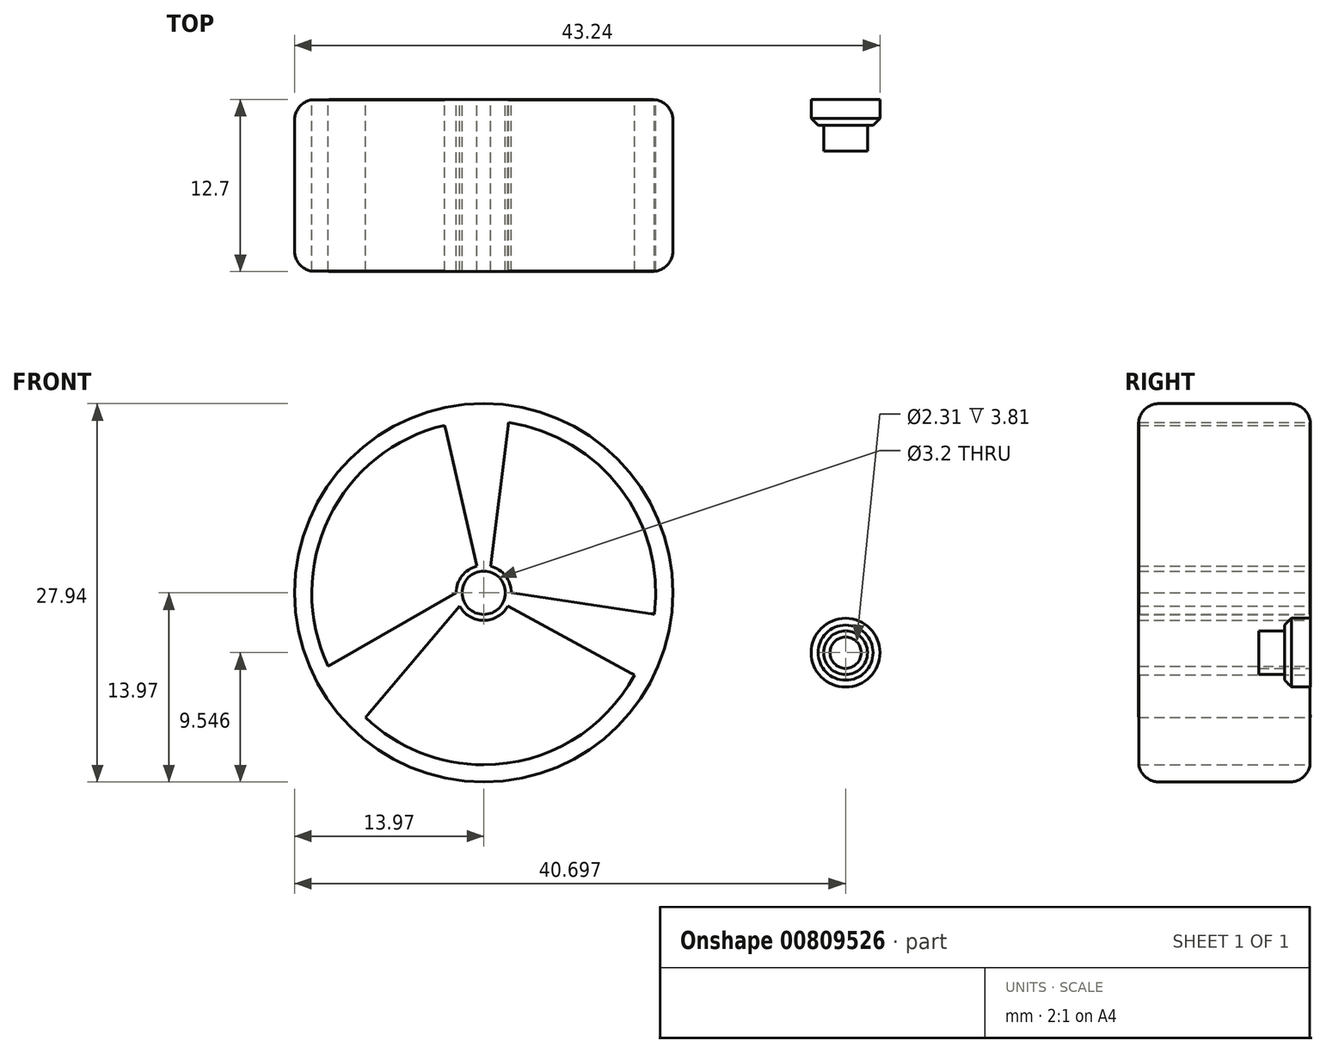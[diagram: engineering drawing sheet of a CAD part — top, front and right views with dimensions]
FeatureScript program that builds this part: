
annotation { "Feature Type Name" : "Feature", "Feature Type Description" : "" }
export const myFeature = defineFeature(function(context is Context, id is Id, definition is map)
    precondition{}
    {
        {
            var Q0;
            Q0=qCreatedBy(makeId("Front.planeOp"),FACE);
            var sketch = newSketch(context, id + "F0", { "sketchPlane" : qUnion([Q0])});
            skCircle(sketch, "E0", {"center": v(0, 0) * mm, "radius": 2.03 * mm});
            skCircle(sketch, "E1", {"center": v(0, 0) * mm, "radius": 12.7 * mm});
            skLineSegment(sketch, "E2", {"start": v(-0.5, 1.97) * mm, "end": v(-2.89, 12.37) * mm});
            skLineSegment(sketch, "E3", {"start": v(0.5, 1.97) * mm, "end": v(1.83, 12.57) * mm});
            skLineSegment(sketch, "E4", {"start": v(2.03, 0) * mm, "end": v(12.6, -1.58) * mm});
            skLineSegment(sketch, "E5", {"start": v(1.78, -0.98) * mm, "end": v(11.15, -6.07) * mm});
            skLineSegment(sketch, "E6", {"start": v(-1.78, -0.98) * mm, "end": v(-8.74, -9.22) * mm});
            skLineSegment(sketch, "E7", {"start": v(-2.03, 0) * mm, "end": v(-11.49, -5.41) * mm});
            skCircle(sketch, "E8", {"center": v(0, 0) * mm, "radius": 13.97 * mm});
            skCircle(sketch, "E9", {"center": v(0, 0) * mm, "radius": 1.6 * mm});
            skSolve(sketch);
        }
        {
            var Q0;
            Q0=makeQuery(id+"F0.imprint","IMPRINT",FACE,{"disambiguationData":[TD([[makeQuery(id+"F0.imprint","IMPRINT",EDGE,{"derivedFrom":sQuery(id+"F0.wireOp",EDGE,"E8")}),1.0]])]});
            var Q1;
            Q1=makeQuery(id+"F0.imprint","IMPRINT",FACE,{"disambiguationData":[TD([[makeQuery(id+"F0.imprint","IMPRINT",EDGE,{"derivedFrom":sQuery(id+"F0.wireOp",EDGE,"E9")}),-1.0]])]});
            var Q2;
            {var subQ0=sQuery(id+"F0.wireOp",EDGE,"E6");Q2=makeQuery(id+"F0.imprint","IMPRINT",FACE,{"disambiguationData":[TD([[makeQuery(id+"F0.imprint","IMPRINT",EDGE,{"derivedFrom":subQ0}),-1.0]])]});}
            var Q3;
            {var subQ0=sQuery(id+"F0.wireOp",EDGE,"E4");Q3=makeQuery(id+"F0.imprint","IMPRINT",FACE,{"disambiguationData":[TD([[makeQuery(id+"F0.imprint","IMPRINT",EDGE,{"derivedFrom":subQ0}),-1.0]])]});}
            var Q4;
            {var subQ0=sQuery(id+"F0.wireOp",EDGE,"E2");Q4=makeQuery(id+"F0.imprint","IMPRINT",FACE,{"disambiguationData":[TD([[makeQuery(id+"F0.imprint","IMPRINT",EDGE,{"derivedFrom":subQ0}),-1.0]])]});}
            extrude(context, id + "F1", {"entities" : qUnion([Q0, Q1, Q2, Q3, Q4]), "depth" : 12.7 * mm, "offsetDistance" : 25.4 * mm});
        }
        {
            var Q0;
            Q0=makeQuery(id+"F1.opExtrude","CAP_EDGE",EDGE,{"disambiguationData":[OSD([sQuery(id+"F0.wireOp",EDGE,"E8")])],"isStart":false});
            var Q1;
            Q1=makeQuery(id+"F1.opExtrude","CAP_EDGE",EDGE,{"disambiguationData":[OSD([sQuery(id+"F0.wireOp",EDGE,"E8")])],"isStart":true});
            fillet(context, id + "F2", {"entities" : qUnion([Q0, Q1]), "radius" : 1.52 * mm, "tangentPropagation" : true, "allowEdgeOverflow" : false});
        }
        {
            var Q0;
            Q0=qCreatedBy(makeId("Front.planeOp"),FACE);
            var sketch = newSketch(context, id + "F3", { "sketchPlane" : qUnion([Q0])});
            skCircle(sketch, "E10", {"center": v(26.73, -4.42) * mm, "radius": 2.54 * mm});
            skCircle(sketch, "E11", {"center": v(26.73, -4.42) * mm, "radius": 1.61 * mm});
            skCircle(sketch, "E12", {"center": v(26.73, -4.42) * mm, "radius": 1.15 * mm});
            skSolve(sketch);
        }
        {
            var Q0;
            Q0=makeQuery(id+"F3.imprint","IMPRINT",FACE,{"disambiguationData":[TD([[makeQuery(id+"F3.imprint","IMPRINT",EDGE,{"derivedFrom":sQuery(id+"F3.wireOp",EDGE,"E11")}),1.0]])]});
            extrude(context, id + "F4", {"entities" : qUnion([Q0]), "depth" : 3.8 * mm, "offsetDistance" : 25.4 * mm});
        }
        {
            var Q0;
            Q0 = qSketchRegion(id + "F3", true);
            extrude(context, id + "F5", {"entities" : qUnion([Q0]), "operationType" : NewBodyOperationType.ADD, "depth" : 1.9 * mm, "offsetDistance" : 25.4 * mm});
        }
        {
            var Q0;
            Q0=makeQuery(id+"F5.opExtrude","CAP_EDGE",EDGE,{"disambiguationData":[OSD([sQuery(id+"F3.wireOp",EDGE,"E10")])],"isStart":false});
            chamfer(context, id + "F6", {"entities" : qUnion([Q0]), "width" : 0.5 * mm, "tangentPropagation" : true});
        }
    });
